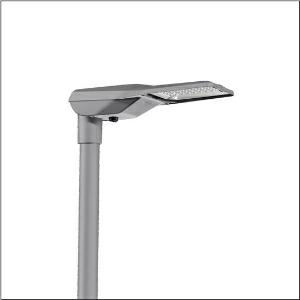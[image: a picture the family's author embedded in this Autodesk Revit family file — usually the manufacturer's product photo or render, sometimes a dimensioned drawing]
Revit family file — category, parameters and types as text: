
# Revit family: streetlight_sl_21_iq_mini___st1_0a_5xe2d31u08jb_b0df
name_source: partatom
category: Lighting Fixtures
units: mm (PartAtom-declared; Revit-internal decimal feet)

## family parameters
Cut with Voids When Loaded = No
Host = Face
Light Source = No
Part Type = Normal
Room Calculation Point = No
Round Connector Dimension = Use Diameter
Shared = No

## types (1)
- --- (1 x LED, 11210 lm, 72.5 W, 3000K)
    Apparent Load = 73 VA
    CIE Flux Codes = 40 73 97 100 100
    Color Rendering = 70
    Color Temperature = 3000K
    Default Elevation = 1800 mm
    Description = Streetlight SL 21 iQ mini, mast luminaire, primary light control with lens, of PMMA, primary optical cover: cover, of toughened safety glass, transparent, light distribution: ST1.0a, light emission: direct distribution, primary light characteristic: asymmetric, installation type: post-top, side-entry, LED, High Power LED, rated luminous flux: 11.210lm, luminous efficacy: 155lm/W, light colour: 730, colour temperature: 3000K, control: presetting dimming logarithmic, Street-Remote, Auto-Match, Temp-Guard, Lumen-Switch, Night-Set, Smart-Wire, Light-Fading, Desk-Remote (wireless, voltage-free reading and setting of iQ features in the workshop via application-optimized NFC function/RFID function), optimised constant luminous flux control (CLO 2.0), mains connection: 220..240V, AC, 50/60Hz, start of lifetime: 73W, end of service life: 76W, reduction: 33W, luminaire housing, of diecast aluminium, powder-coated, Siteco® metallic grey (DB 702S), corrosivity category C5 mid according to DIN EN ISO 12944, please order mast flange separately, inclination adjustable: 0°, 5°, 10°, 15°, sealing non-destructively replaceable, multi-level sealing system, length: 628mm, width: 235mm, height: 110mm, mast flange for spigot size: 42mm (side-entry): 5XC10008XM4, 60/48mm (side-entry/post-top): 5XC10108XM2, 76/60mm (side-entry/post-top): 5XC10108XM1, Smart Interface below, protection rating (complete): IP66, insulation class (complete): insulation class II (safety insulation), certification: CE, ENEC, ENEC+, VDE, impact resistance: IK09, permissible operating ambient temperature for outdoor applications: -40..+50°C, standard-compliant lighting for roads and squares, packaging unit: 1 piece

Light Distribution: ST1.0a
    Height = 110 mm
    Lamp = 1 x LED
    Lamp Light Flux = 11210 lm
    Lamp Power = 72.5 W
    Lamp count = 1
    Length = 625 mm
    Luminous efficacy = 155 lm/W
    Manufacturer = Siteco
    ModVariant = No
    Model = 5XE2D31U08JB
    Number of Poles = 1
    OnlyDefault = Yes
    Power Factor = 1
    Product Name = Streetlight SL 21 iQ mini | ST1.0a
    Product group = mast luminaire | pylon top
    ProductGroupID = 6100
    Protection Class = Protection class II
    Protection Degree = IP 66
    RLX_Detail_Level = 1
    RLX_Emergency_Light_Flux = 0 lm
    RLX_Emergency_Type = 0
    RLX_Emergency_Type_DB = No
    RlxData = <blob elided: 92625 chars, md5=3872b9e4>
    Socket = socket
    Standby Power = 0 W
    System Light Flux = 11210 lm
    System Power = 73 W
    Type Comments = factory setting: luminous flux: 100 % | dim-lin: 254 | 755 mA
    Type Image = l_1003516.jpg
    URL = http://relux.com
    VarID = @adj_044263
    Voltage = 0 V
    Weight = 0.00 kg
    Width = 234 mm

## geometry (parser evidence)
native form markers: Blend x4, Sweep x12
no freeform markers — native parametric forms only
